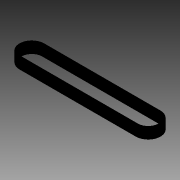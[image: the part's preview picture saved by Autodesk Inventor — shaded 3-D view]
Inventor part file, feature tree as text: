
AUTODESK INVENTOR PART (.ipt)
format: ipt  version: 2013 (Build 170138000, 138)  size: 91,648 bytes
history: native  units: mm
features: extrude x1, sketch x1
ambient origin geometry x8: Origin, YZ Plane, XZ Plane, XY Plane, X Axis, Y Axis, Z Axis, Center Point
bodies: Solid1 (feature_tree)
feature tree (2):
  extrude  "Extrusion1"  Depth=12.0mm
  sketch  "Sketch1"  dims[d0=12.0mm d2=12.0mm d3=68.0mm d4=1.2mm d5=6.0mm d6=0.0mm]
